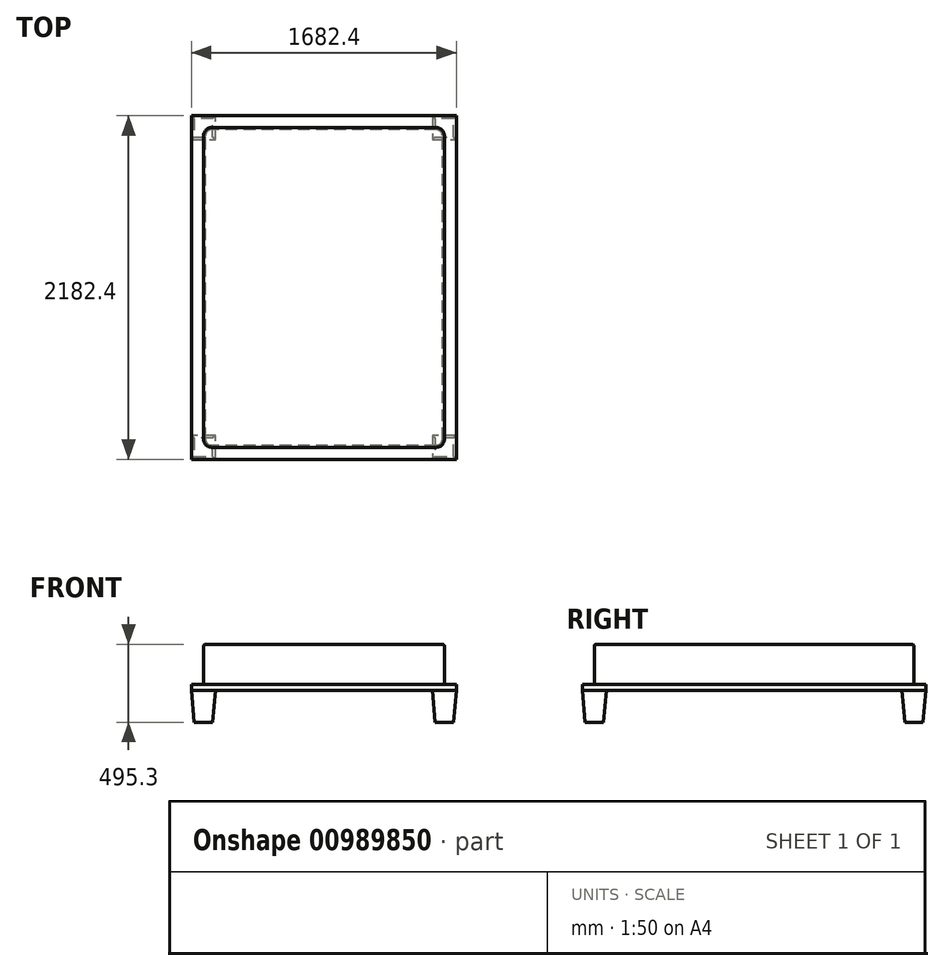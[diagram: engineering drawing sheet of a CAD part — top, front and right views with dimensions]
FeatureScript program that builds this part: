
annotation { "Feature Type Name" : "Feature", "Feature Type Description" : "" }
export const myFeature = defineFeature(function(context is Context, id is Id, definition is map)
    precondition{}
    {
        {
            var Q0;
            Q0=qCreatedBy(makeId("Top.planeOp"),FACE);
            var sketch = newSketch(context, id + "F0", { "sketchPlane" : qUnion([Q0])});
            skLineSegment(sketch, "E0.bottom", {"start": v(765, -1015) * mm, "end": v(-765, -1015) * mm});
            skLineSegment(sketch, "E0.top", {"start": v(765, 1015) * mm, "end": v(-765, 1015) * mm});
            skLineSegment(sketch, "E0.left", {"start": v(765, -1015) * mm, "end": v(765, 1015) * mm});
            skLineSegment(sketch, "E0.right", {"start": v(-765, -1015) * mm, "end": v(-765, 1015) * mm});
            skPoint(sketch, "E0.middle", {"position": v(0, 0) * mm});
            skSolve(sketch);
        }
        {
            var Q0;
            Q0 = qSketchRegion(id + "F0", true);
            extrude(context, id + "F1", {"entities" : qUnion([Q0]), "depth" : 254 * mm, "offsetDistance" : 30.48 * mm});
        }
        {
            var Q0;
            Q0=makeQuery(id+"F1.opExtrude","SWEPT_EDGE",EDGE,{"disambiguationData":[OSD([sQuery(id+"F0.wireOp",EDGE,"E0.bottom"),sQuery(id+"F0.wireOp",EDGE,"E0.right")])]});
            var Q1;
            Q1=makeQuery(id+"F1.opExtrude","SWEPT_EDGE",EDGE,{"disambiguationData":[OSD([sQuery(id+"F0.wireOp",EDGE,"E0.bottom"),sQuery(id+"F0.wireOp",EDGE,"E0.left")])]});
            var Q2;
            Q2=makeQuery(id+"F1.opExtrude","SWEPT_EDGE",EDGE,{"disambiguationData":[OSD([sQuery(id+"F0.wireOp",EDGE,"E0.top"),sQuery(id+"F0.wireOp",EDGE,"E0.left")])]});
            var Q3;
            Q3=makeQuery(id+"F1.opExtrude","SWEPT_EDGE",EDGE,{"disambiguationData":[OSD([sQuery(id+"F0.wireOp",EDGE,"E0.top"),sQuery(id+"F0.wireOp",EDGE,"E0.right")])]});
            fillet(context, id + "F2", {"entities" : qUnion([Q0, Q1, Q2, Q3]), "radius" : 50.8 * mm, "tangentPropagation" : true, "allowEdgeOverflow" : false});
        }
        {
            var Q0;
            Q0=makeQuery(id+"F1.opExtrude","CAP_FACE",FACE,{"disambiguationData":[OSD([sQuery(id+"F0.wireOp",EDGE,"E0.bottom"),sQuery(id+"F0.wireOp",EDGE,"E0.top"),sQuery(id+"F0.wireOp",EDGE,"E0.left"),sQuery(id+"F0.wireOp",EDGE,"E0.right")])],"isStart":false});
            var Q1;
            Q1=makeQuery(id+"F1.opExtrude","CAP_FACE",FACE,{"disambiguationData":[OSD([sQuery(id+"F0.wireOp",EDGE,"E0.bottom"),sQuery(id+"F0.wireOp",EDGE,"E0.top"),sQuery(id+"F0.wireOp",EDGE,"E0.left"),sQuery(id+"F0.wireOp",EDGE,"E0.right")])],"isStart":true});
            fillet(context, id + "F3", {"entities" : qUnion([Q0, Q1]), "radius" : 12.7 * mm, "tangentPropagation" : true, "allowEdgeOverflow" : false});
        }
        {
            var Q0;
            Q0=makeQuery(id+"F1.opExtrude","CAP_FACE",FACE,{"disambiguationData":[OSD([sQuery(id+"F0.wireOp",EDGE,"E0.bottom"),sQuery(id+"F0.wireOp",EDGE,"E0.top"),sQuery(id+"F0.wireOp",EDGE,"E0.left"),sQuery(id+"F0.wireOp",EDGE,"E0.right")])],"isStart":true});
            var sketch = newSketch(context, id + "F4", { "sketchPlane" : qUnion([Q0])});
            skLineSegment(sketch, "E1.bottom", {"start": v(841.2, -1091.2) * mm, "end": v(-841.2, -1091.2) * mm});
            skLineSegment(sketch, "E1.top", {"start": v(841.2, 1091.2) * mm, "end": v(-841.2, 1091.2) * mm});
            skLineSegment(sketch, "E1.left", {"start": v(841.2, -1091.2) * mm, "end": v(841.2, 1091.2) * mm});
            skLineSegment(sketch, "E1.right", {"start": v(-841.2, -1091.2) * mm, "end": v(-841.2, 1091.2) * mm});
            skPoint(sketch, "E1.middle", {"position": v(0, 0) * mm});
            skSolve(sketch);
        }
        {
            var Q0;
            Q0 = qSketchRegion(id + "F4", true);
            extrude(context, id + "F5", {"entities" : qUnion([Q0]), "operationType" : NewBodyOperationType.ADD, "depth" : 38.1 * mm, "offsetDistance" : 30.48 * mm});
        }
        {
            var Q0;
            Q0=makeQuery(id+"F5.opExtrude","CAP_FACE",FACE,{"disambiguationData":[OSD([sQuery(id+"F4.wireOp",EDGE,"E1.bottom"),sQuery(id+"F4.wireOp",EDGE,"E1.top"),sQuery(id+"F4.wireOp",EDGE,"E1.left"),sQuery(id+"F4.wireOp",EDGE,"E1.right")])],"isStart":false});
            var sketch = newSketch(context, id + "F6", { "sketchPlane" : qUnion([Q0])});
            skLineSegment(sketch, "E2.bottom", {"start": v(-841.2, 1091.2) * mm, "end": v(-688.8, 1091.2) * mm});
            skLineSegment(sketch, "E2.top", {"start": v(-841.2, 938.8) * mm, "end": v(-688.8, 938.8) * mm});
            skLineSegment(sketch, "E2.left", {"start": v(-841.2, 1091.2) * mm, "end": v(-841.2, 938.8) * mm});
            skLineSegment(sketch, "E2.right", {"start": v(-688.8, 1091.2) * mm, "end": v(-688.8, 938.8) * mm});
            skLineSegment(sketch, "E3.bottom", {"start": v(841.2, 1091.2) * mm, "end": v(688.8, 1091.2) * mm});
            skLineSegment(sketch, "E3.top", {"start": v(841.2, 938.8) * mm, "end": v(688.8, 938.8) * mm});
            skLineSegment(sketch, "E3.left", {"start": v(841.2, 1091.2) * mm, "end": v(841.2, 938.8) * mm});
            skLineSegment(sketch, "E3.right", {"start": v(688.8, 1091.2) * mm, "end": v(688.8, 938.8) * mm});
            skLineSegment(sketch, "E4.bottom", {"start": v(841.2, -1091.2) * mm, "end": v(688.8, -1091.2) * mm});
            skLineSegment(sketch, "E4.top", {"start": v(841.2, -938.8) * mm, "end": v(688.8, -938.8) * mm});
            skLineSegment(sketch, "E4.left", {"start": v(841.2, -1091.2) * mm, "end": v(841.2, -938.8) * mm});
            skLineSegment(sketch, "E4.right", {"start": v(688.8, -1091.2) * mm, "end": v(688.8, -938.8) * mm});
            skLineSegment(sketch, "E5.bottom", {"start": v(-841.2, -1091.2) * mm, "end": v(-688.8, -1091.2) * mm});
            skLineSegment(sketch, "E5.top", {"start": v(-841.2, -938.8) * mm, "end": v(-688.8, -938.8) * mm});
            skLineSegment(sketch, "E5.left", {"start": v(-841.2, -1091.2) * mm, "end": v(-841.2, -938.8) * mm});
            skLineSegment(sketch, "E5.right", {"start": v(-688.8, -1091.2) * mm, "end": v(-688.8, -938.8) * mm});
            skSolve(sketch);
        }
        {
            var Q0;
            Q0 = qSketchRegion(id + "F6", true);
            extrude(context, id + "F7", {"entities" : qUnion([Q0]), "operationType" : NewBodyOperationType.ADD, "depth" : 203.2 * mm, "offsetDistance" : 30.48 * mm, "hasDraft" : true, "draftAngle" : 5 * degree, "draftPullDirection" : true});
        }
    });
